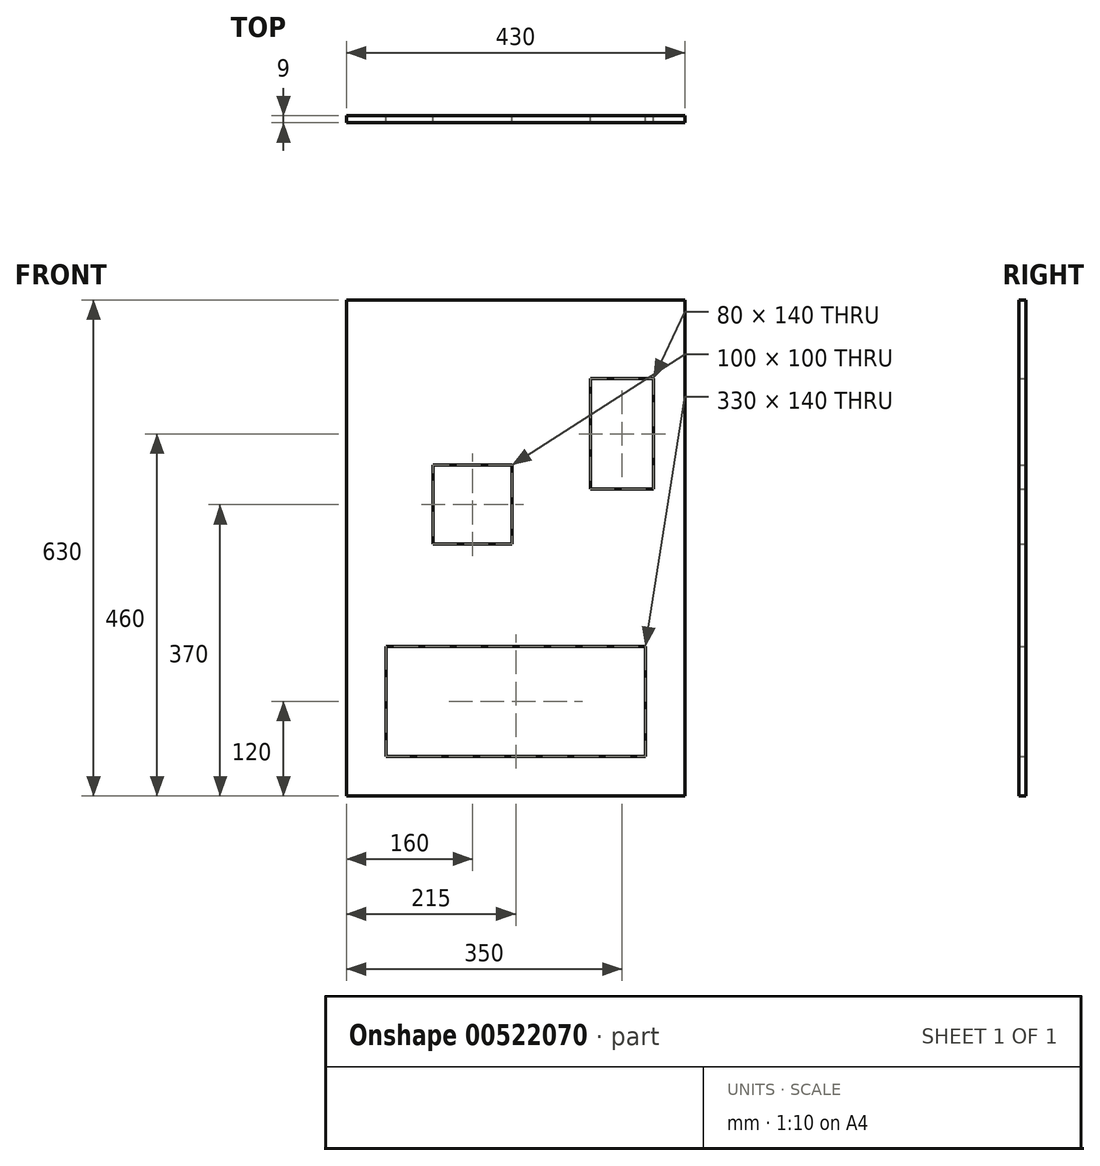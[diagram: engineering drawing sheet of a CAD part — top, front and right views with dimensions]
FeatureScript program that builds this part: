
annotation { "Feature Type Name" : "Feature", "Feature Type Description" : "" }
export const myFeature = defineFeature(function(context is Context, id is Id, definition is map)
    precondition{}
    {
        {
            var Q0;
            Q0=qCreatedBy(makeId("Front.planeOp"),FACE);
            var sketch = newSketch(context, id + "F0", { "sketchPlane" : qUnion([Q0])});
            skLineSegment(sketch, "E0.bottom", {"start": v(0, 0) * mm, "end": v(-430, 0) * mm});
            skLineSegment(sketch, "E0.top", {"start": v(0, 630) * mm, "end": v(-430, 630) * mm});
            skLineSegment(sketch, "E0.left", {"start": v(0, 0) * mm, "end": v(0, 630) * mm});
            skLineSegment(sketch, "E0.right", {"start": v(-430, 0) * mm, "end": v(-430, 630) * mm});
            skSolve(sketch);
        }
        {
            var Q0;
            Q0=makeQuery(id+"F0.imprint","IMPRINT",FACE,{"disambiguationData":[TD([[makeQuery(id+"F0.imprint","IMPRINT",EDGE,{"derivedFrom":sQuery(id+"F0.wireOp",EDGE,"E0.bottom")}),-1.0]])]});
            extrude(context, id + "F1", {"entities" : qUnion([Q0]), "depth" : 9 * mm, "offsetDistance" : 25 * mm});
        }
        {
            var Q0;
            Q0=makeQuery(id+"F1.opExtrude","CAP_FACE",FACE,{"disambiguationData":[OSD([sQuery(id+"F0.wireOp",EDGE,"E0.bottom"),sQuery(id+"F0.wireOp",EDGE,"E0.top"),sQuery(id+"F0.wireOp",EDGE,"E0.left"),sQuery(id+"F0.wireOp",EDGE,"E0.right")])],"isStart":true});
            var sketch = newSketch(context, id + "F2", { "sketchPlane" : qUnion([Q0])});
            skLineSegment(sketch, "E1.bottom", {"start": v(380, 190) * mm, "end": v(50, 190) * mm});
            skLineSegment(sketch, "E1.top", {"start": v(380, 50) * mm, "end": v(50, 50) * mm});
            skLineSegment(sketch, "E1.left", {"start": v(380, 190) * mm, "end": v(380, 50) * mm});
            skLineSegment(sketch, "E1.right", {"start": v(50, 190) * mm, "end": v(50, 50) * mm});
            skLineSegment(sketch, "E2.bottom", {"start": v(320, 420) * mm, "end": v(220, 420) * mm});
            skLineSegment(sketch, "E2.top", {"start": v(320, 320) * mm, "end": v(220, 320) * mm});
            skLineSegment(sketch, "E2.left", {"start": v(320, 420) * mm, "end": v(320, 320) * mm});
            skLineSegment(sketch, "E2.right", {"start": v(220, 420) * mm, "end": v(220, 320) * mm});
            skLineSegment(sketch, "E3.bottom", {"start": v(120, 530) * mm, "end": v(40, 530) * mm});
            skLineSegment(sketch, "E3.top", {"start": v(120, 390) * mm, "end": v(40, 390) * mm});
            skLineSegment(sketch, "E3.left", {"start": v(120, 530) * mm, "end": v(120, 390) * mm});
            skLineSegment(sketch, "E3.right", {"start": v(40, 530) * mm, "end": v(40, 390) * mm});
            skSolve(sketch);
        }
        {
            var Q0;
            Q0 = qSketchRegion(id + "F2", true);
            extrude(context, id + "F3", {"entities" : qUnion([Q0]), "operationType" : NewBodyOperationType.REMOVE, "oppositeDirection" : true, "depth" : 25 * mm, "offsetDistance" : 25 * mm});
        }
    });
